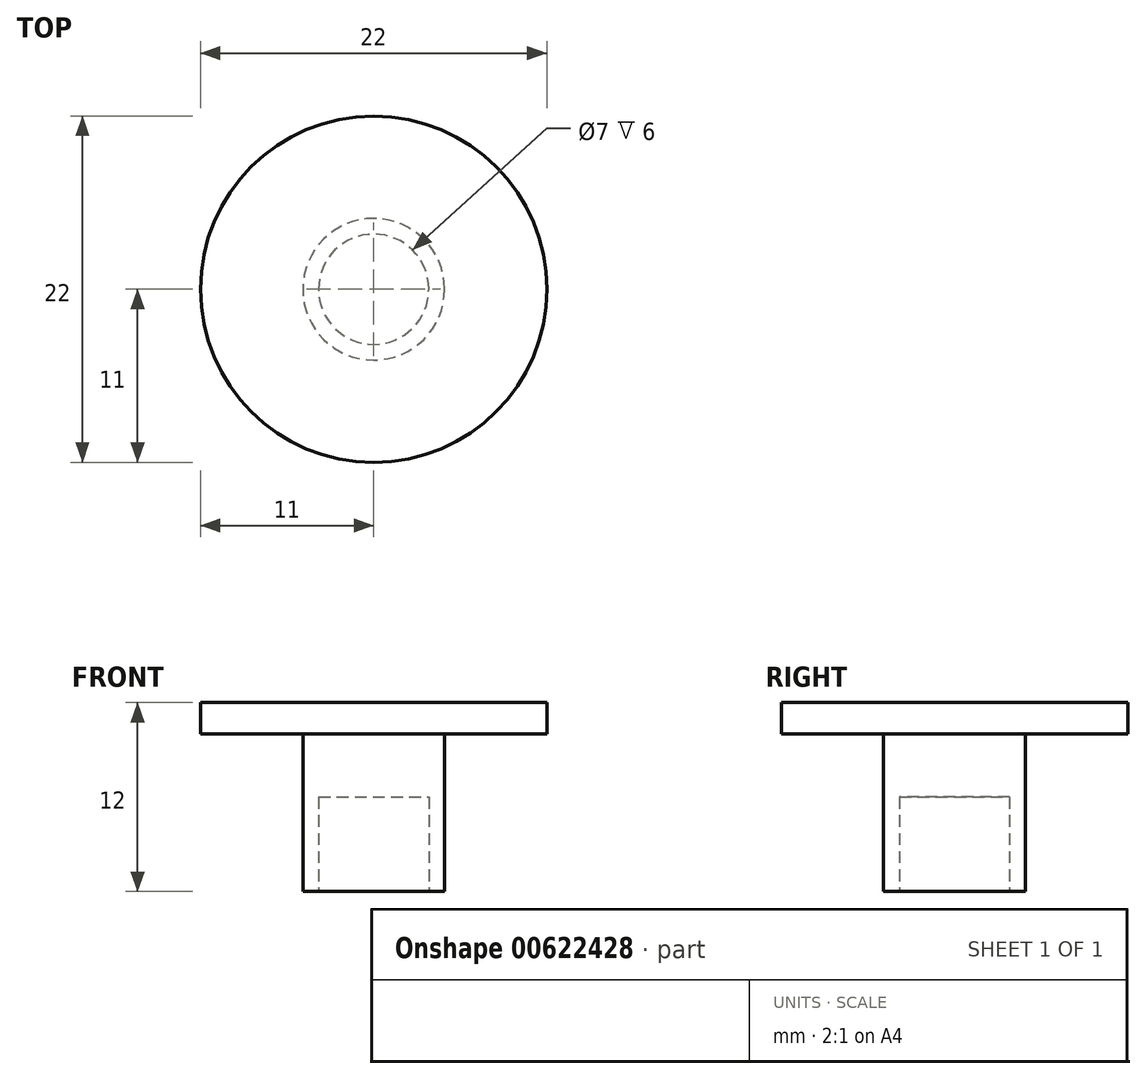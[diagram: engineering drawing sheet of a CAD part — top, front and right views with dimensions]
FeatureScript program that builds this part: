
annotation { "Feature Type Name" : "Feature", "Feature Type Description" : "" }
export const myFeature = defineFeature(function(context is Context, id is Id, definition is map)
    precondition{}
    {
        {
            var Q0;
            Q0=qCreatedBy(makeId("Top.planeOp"),FACE);
            var sketch = newSketch(context, id + "F0", { "sketchPlane" : qUnion([Q0])});
            skCircle(sketch, "E0", {"center": v(0, 0) * mm, "radius": 4.5 * mm});
            skSolve(sketch);
        }
        {
            var Q0;
            Q0=makeQuery(id+"F0.imprint","IMPRINT",FACE,{"disambiguationData":[TD([[makeQuery(id+"F0.imprint","IMPRINT",EDGE,{"derivedFrom":sQuery(id+"F0.wireOp",EDGE,"E0")}),1.0]])]});
            extrude(context, id + "F1", {"entities" : qUnion([Q0]), "depth" : 10 * mm, "offsetDistance" : 25 * mm});
        }
        {
            var Q0;
            Q0=makeQuery(id+"F1.opExtrude","CAP_FACE",FACE,{"disambiguationData":[OSD([sQuery(id+"F0.wireOp",EDGE,"E0")])],"isStart":false});
            var sketch = newSketch(context, id + "F2", { "sketchPlane" : qUnion([Q0])});
            skCircle(sketch, "E1", {"center": v(0, 0) * mm, "radius": 11 * mm});
            skSolve(sketch);
        }
        {
            var Q0;
            Q0=makeQuery(id+"F2.imprint","IMPRINT",FACE,{"disambiguationData":[TD([[makeQuery(id+"F2.imprint","IMPRINT",EDGE,{"derivedFrom":sQuery(id+"F2.wireOp",EDGE,"E1")}),1.0]])]});
            var Q1;
            Q1=makeQuery(id+"F2.imprint","IMPRINT",FACE,{"disambiguationData":[TD([[makeQuery(id+"F2.imprint","IMPRINT",EDGE,{"derivedFrom":makeQuery(id+"F1.opExtrude","CAP_EDGE",EDGE,{"disambiguationData":[OSD([sQuery(id+"F0.wireOp",EDGE,"E0")])],"isStart":false})}),1.0]])]});
            extrude(context, id + "F3", {"entities" : qUnion([Q0, Q1]), "operationType" : NewBodyOperationType.ADD, "depth" : 2 * mm, "offsetDistance" : 25 * mm});
        }
        {
            var Q0;
            Q0=makeQuery(id+"F1.opExtrude","CAP_FACE",FACE,{"disambiguationData":[OSD([sQuery(id+"F0.wireOp",EDGE,"E0")])],"isStart":true});
            var sketch = newSketch(context, id + "F4", { "sketchPlane" : qUnion([Q0])});
            skCircle(sketch, "E2", {"center": v(0, 0) * mm, "radius": 3.5 * mm});
            skSolve(sketch);
        }
        {
            var Q0;
            Q0=makeQuery(id+"F4.imprint","IMPRINT",FACE,{"disambiguationData":[TD([[makeQuery(id+"F4.imprint","IMPRINT",EDGE,{"derivedFrom":sQuery(id+"F4.wireOp",EDGE,"E2")}),1.0]])]});
            extrude(context, id + "F5", {"entities" : qUnion([Q0]), "operationType" : NewBodyOperationType.REMOVE, "oppositeDirection" : true, "depth" : 6 * mm, "offsetDistance" : 25 * mm});
        }
    });
